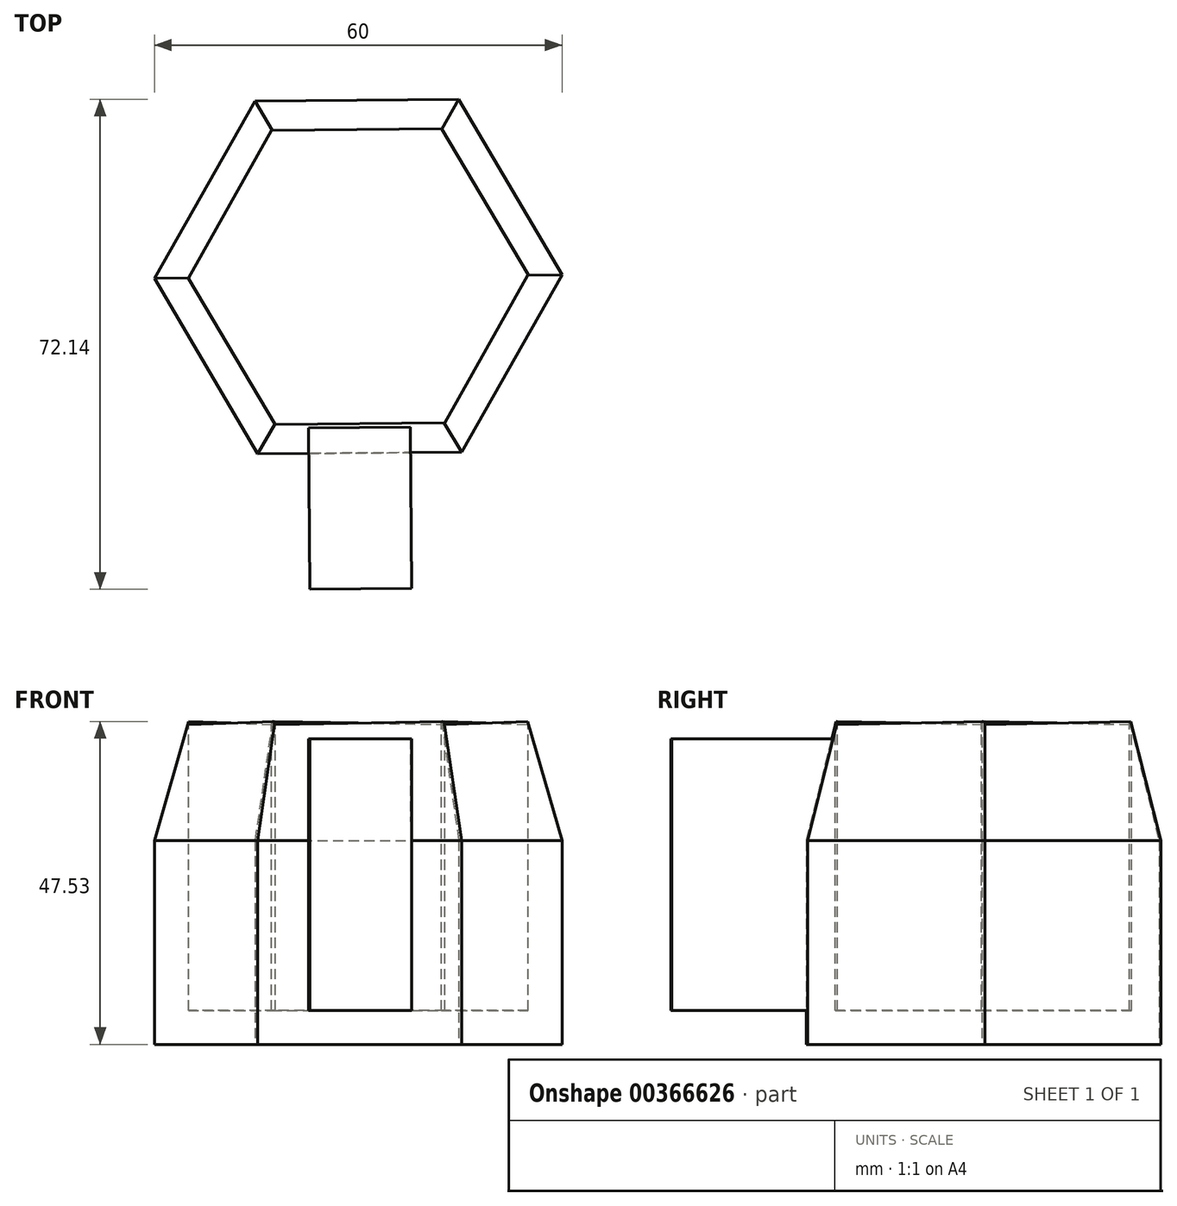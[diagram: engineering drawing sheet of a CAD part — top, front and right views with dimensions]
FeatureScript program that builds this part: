
annotation { "Feature Type Name" : "Feature", "Feature Type Description" : "" }
export const myFeature = defineFeature(function(context is Context, id is Id, definition is map)
    precondition{}
    {
        {
            var Q0;
            Q0=qCreatedBy(makeId("Top.planeOp"),FACE);
            var sketch = newSketch(context, id + "F0", { "sketchPlane" : qUnion([Q0])});
            skCircle(sketch, "E0.cCircle", {"center": v(0, 0) * mm, "radius": 25.98 * mm, "construction": true});
            skLineSegment(sketch, "E0.0", {"start": v(14.8, 26.1) * mm, "end": v(30, 0.24) * mm});
            skLineSegment(sketch, "E0.1", {"start": v(30, 0.24) * mm, "end": v(15.2, -25.86) * mm});
            skLineSegment(sketch, "E0.2", {"start": v(15.2, -25.86) * mm, "end": v(-14.8, -26.1) * mm});
            skLineSegment(sketch, "E0.3", {"start": v(-14.8, -26.1) * mm, "end": v(-30, -0.24) * mm});
            skLineSegment(sketch, "E0.4", {"start": v(-30, -0.24) * mm, "end": v(-15.2, 25.86) * mm});
            skLineSegment(sketch, "E0.5", {"start": v(-15.2, 25.86) * mm, "end": v(14.8, 26.1) * mm});
            skPoint(sketch, "E0.0.midPoint", {"position": v(22.4, 13.17) * mm});
            skSolve(sketch);
        }
        {
            var Q0;
            Q0=makeQuery(id+"F0.imprint","IMPRINT",FACE,{"disambiguationData":[TD([[makeQuery(id+"F0.imprint","IMPRINT",EDGE,{"derivedFrom":sQuery(id+"F0.wireOp",EDGE,"E0.0")}),-1.0]])]});
            extrude(context, id + "F1", {"entities" : qUnion([Q0]), "depth" : 50 * mm});
        }
        {
            var Q0;
            Q0=makeQuery(id+"F1.opExtrude","CAP_FACE",FACE,{"disambiguationData":[OSD([sQuery(id+"F0.wireOp",EDGE,"E0.0"),sQuery(id+"F0.wireOp",EDGE,"E0.1"),sQuery(id+"F0.wireOp",EDGE,"E0.2"),sQuery(id+"F0.wireOp",EDGE,"E0.3"),sQuery(id+"F0.wireOp",EDGE,"E0.4"),sQuery(id+"F0.wireOp",EDGE,"E0.5")])],"isStart":false});
            var sketch = newSketch(context, id + "F2", { "sketchPlane" : qUnion([Q0])});
            skCircle(sketch, "E1.cCircle", {"center": v(0, 0) * mm, "radius": 21.65 * mm, "construction": true});
            skLineSegment(sketch, "E1.0", {"start": v(12.23, 21.8) * mm, "end": v(25, 0.3) * mm});
            skLineSegment(sketch, "E1.1", {"start": v(25, 0.3) * mm, "end": v(12.76, -21.5) * mm});
            skLineSegment(sketch, "E1.2", {"start": v(12.76, -21.5) * mm, "end": v(-12.23, -21.8) * mm});
            skLineSegment(sketch, "E1.3", {"start": v(-12.23, -21.8) * mm, "end": v(-25, -0.3) * mm});
            skLineSegment(sketch, "E1.4", {"start": v(-25, -0.3) * mm, "end": v(-12.76, 21.5) * mm});
            skLineSegment(sketch, "E1.5", {"start": v(-12.76, 21.5) * mm, "end": v(12.23, 21.8) * mm});
            skPoint(sketch, "E1.0.midPoint", {"position": v(18.62, 11.05) * mm});
            skSolve(sketch);
        }
        {
            var Q0;
            Q0=makeQuery(id+"F2.imprint","IMPRINT",FACE,{"disambiguationData":[TD([[makeQuery(id+"F2.imprint","IMPRINT",EDGE,{"derivedFrom":sQuery(id+"F2.wireOp",EDGE,"E1.0")}),-1.0]])]});
            extrude(context, id + "F3", {"entities" : qUnion([Q0]), "operationType" : NewBodyOperationType.REMOVE, "oppositeDirection" : true, "depth" : 45 * mm});
        }
        {
            var Q0;
            Q0=makeQuery(id+"F1.opExtrude","SWEPT_FACE",FACE,{"disambiguationData":[OSD([sQuery(id+"F0.wireOp",EDGE,"E0.2")])]});
            var sketch = newSketch(context, id + "F4", { "sketchPlane" : qUnion([Q0])});
            skLineSegment(sketch, "E2.bottom", {"start": v(-7.5, 45) * mm, "end": v(7.5, 45) * mm});
            skLineSegment(sketch, "E2.top", {"start": v(-7.5, 5) * mm, "end": v(7.5, 5) * mm});
            skLineSegment(sketch, "E2.left", {"start": v(-7.5, 45) * mm, "end": v(-7.5, 5) * mm});
            skLineSegment(sketch, "E2.right", {"start": v(7.5, 45) * mm, "end": v(7.5, 5) * mm});
            skSolve(sketch);
        }
        {
            var Q0;
            Q0=makeQuery(id+"F4.imprint","IMPRINT",FACE,{"disambiguationData":[TD([[makeQuery(id+"F4.imprint","IMPRINT",EDGE,{"derivedFrom":sQuery(id+"F4.wireOp",EDGE,"E2.bottom")}),-1.0]])]});
            extrude(context, id + "F5", {"entities" : qUnion([Q0]), "operationType" : NewBodyOperationType.ADD, "depth" : 20 * mm});
        }
        {
            var Q0;
            Q0=makeQuery(id+"F1.opExtrude","CAP_EDGE",EDGE,{"disambiguationData":[OSD([sQuery(id+"F0.wireOp",EDGE,"E0.1")])],"isStart":false});
            var Q1;
            Q1=makeQuery(id+"F1.opExtrude","CAP_EDGE",EDGE,{"disambiguationData":[OSD([sQuery(id+"F0.wireOp",EDGE,"E0.2")])],"isStart":false});
            var Q2;
            Q2=makeQuery(id+"F1.opExtrude","CAP_EDGE",EDGE,{"disambiguationData":[OSD([sQuery(id+"F0.wireOp",EDGE,"E0.3")])],"isStart":false});
            var Q3;
            Q3=makeQuery(id+"F1.opExtrude","CAP_EDGE",EDGE,{"disambiguationData":[OSD([sQuery(id+"F0.wireOp",EDGE,"E0.4")])],"isStart":false});
            var Q4;
            Q4=makeQuery(id+"F1.opExtrude","CAP_EDGE",EDGE,{"disambiguationData":[OSD([sQuery(id+"F0.wireOp",EDGE,"E0.5")])],"isStart":false});
            var Q5;
            Q5=makeQuery(id+"F1.opExtrude","CAP_EDGE",EDGE,{"disambiguationData":[OSD([sQuery(id+"F0.wireOp",EDGE,"E0.0")])],"isStart":false});
            chamfer(context, id + "F6", {"entities" : qUnion([Q0, Q1, Q2, Q3, Q4, Q5]), "chamferType" : ChamferType.TWO_OFFSETS, "width1" : 20 * mm, "oppositeDirection" : false, "width2" : 5 * mm, "tangentPropagation" : true});
        }
    });
